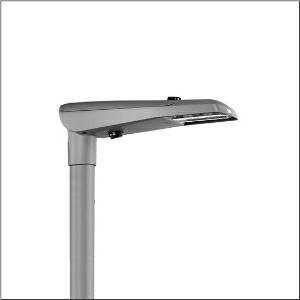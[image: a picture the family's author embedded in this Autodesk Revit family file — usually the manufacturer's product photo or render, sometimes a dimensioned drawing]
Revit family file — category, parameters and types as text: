
# Revit family: streetlight_sl_11_iq_micro___st1_2a_5xc1ac1y08de_0507
name_source: partatom
category: Lighting Fixtures
units: mm (PartAtom-declared; Revit-internal decimal feet)

## family parameters
Cut with Voids When Loaded = No
Host = Face
Light Source = No
Part Type = Normal
Room Calculation Point = No
Round Connector Dimension = Use Diameter
Shared = No

## types (1)
- --- (1 x LED, 3860 lm, 27.3 W, 4000K)
    Apparent Load = 27 VA
    CIE Flux Codes = 33 71 96 100 100
    Color Rendering = 70
    Color Temperature = 4000K
    Default Elevation = 1800 mm
    Description = Streetlight SL 11 iQ micro, mast luminaire, primary light control with 3 zone facetted reflector, of plastic, silver coated, highly specular, primary optical cover: cover, of PMMA, transparent, light distribution: ST1.2a, light emission: direct distribution, primary light characteristic: asymmetric, installation type: post-top, side-entry, lamps: LED, High Power LED, rated values: 3.620lm | 27,1W | 133,6lm/W (begin service life); end service life: 3.620lm | 27,6W; at 50% lumin. flux: 1.810lm | 13,3W | 136,1lm/W, colour temperature: 2200/2700/3000/4000K, colour rendering: CRI > 70, light colour: 722/727/730/740, light setting 1 begin service life: 100% | 3.620lm | 27,1W | 133,6lm/W | 3.000K, light setting 1 end service life: 27,6W, further light settings possible, control: pre-setting: logarithmic dimming characteristic, Street-Remote, Auto-Match, Temp-Guard, Lumen-Switch, Night-Set, Smart-Wire, Light-Fading, Desk-Remote (wireless, voltage-free reading and setting of iQ features in the workshop via application-optimized NFC function/RFID function), optimised constant luminous flux control (CLO 2.0), with cable H07RN-F 5x 1.5mm², mains connection: 220..240V, AC, 50/60Hz, connection cable pre-assembled, cable length: 6,5m, luminaire housing, of diecast aluminium, powder-coated, Siteco® metallic grey (DB 702S), please order mast flange separately, inclination adjustable without tools: 0°, 5°, 10°, 15° (post-top) | 0°, -5°, -10°, -15° (side-entry), sealing non-destructively replaceable, multi-level sealing system, length: 600mm, width: 174mm, height: 116mm, mast flange for spigot size: 42mm (side-entry): 5XC10008XM4, 60/48mm (side-entry/post-top): 5XC10108XM2, 76/60mm (side-entry/post-top): 5XC10108XM1, equipment: Power, Smart Interface below and above, protection rating (complete): IP66, insulation class (complete): insulation class II (safety insulation), certification: CE, ENEC, ENEC+, VDE, UKCA, impact resistance: IK10, permissible operating ambient temperature for outdoor applications: -25..+50°C, standard-compliant lighting for roads and squares, Environmental Product Declaration (EPD) tested and certified by an independent institute, packaging unit: 1 piece

Light Distribution: ST1.2a
    Height = 116 mm
    Lamp = 1 x LED
    Lamp Light Flux = 3860 lm
    Lamp Power = 27.3 W
    Lamp count = 1
    Length = 600 mm
    Luminous efficacy = 141 lm/W
    Manufacturer = Siteco
    ModVariant = No
    Model = 5XC1AC1Y08DE
    Number of Poles = 1
    OnlyDefault = Yes
    Power Factor = 1
    Product Name = Streetlight SL 11 iQ micro | ST1.2a
    Product group = mast luminaire | pylon top
    ProductGroupID = 6100
    Protection Class = Protection class II
    Protection Degree = IP 66
    RLX_Detail_Level = 1
    RLX_Emergency_Light_Flux = 0 lm
    RLX_Emergency_Type = 0
    RLX_Emergency_Type_DB = No
    RlxData = <blob elided: 59501 chars, md5=11995b61>
    Socket = socket
    Standby Power = 0 W
    System Light Flux = 3860 lm
    System Power = 27 W
    Type Comments = individual setting: luminous flux: 100 % | dim-lin: 254 | 726 mA
    Type Image = l_1005956.jpg
    URL = http://relux.com
    VarID = @adj_044704
    Voltage = 0 V
    Weight = 0.00 kg
    Width = 174 mm

## geometry (parser evidence)
native form markers: Blend x4, Sweep x12
no freeform markers — native parametric forms only
